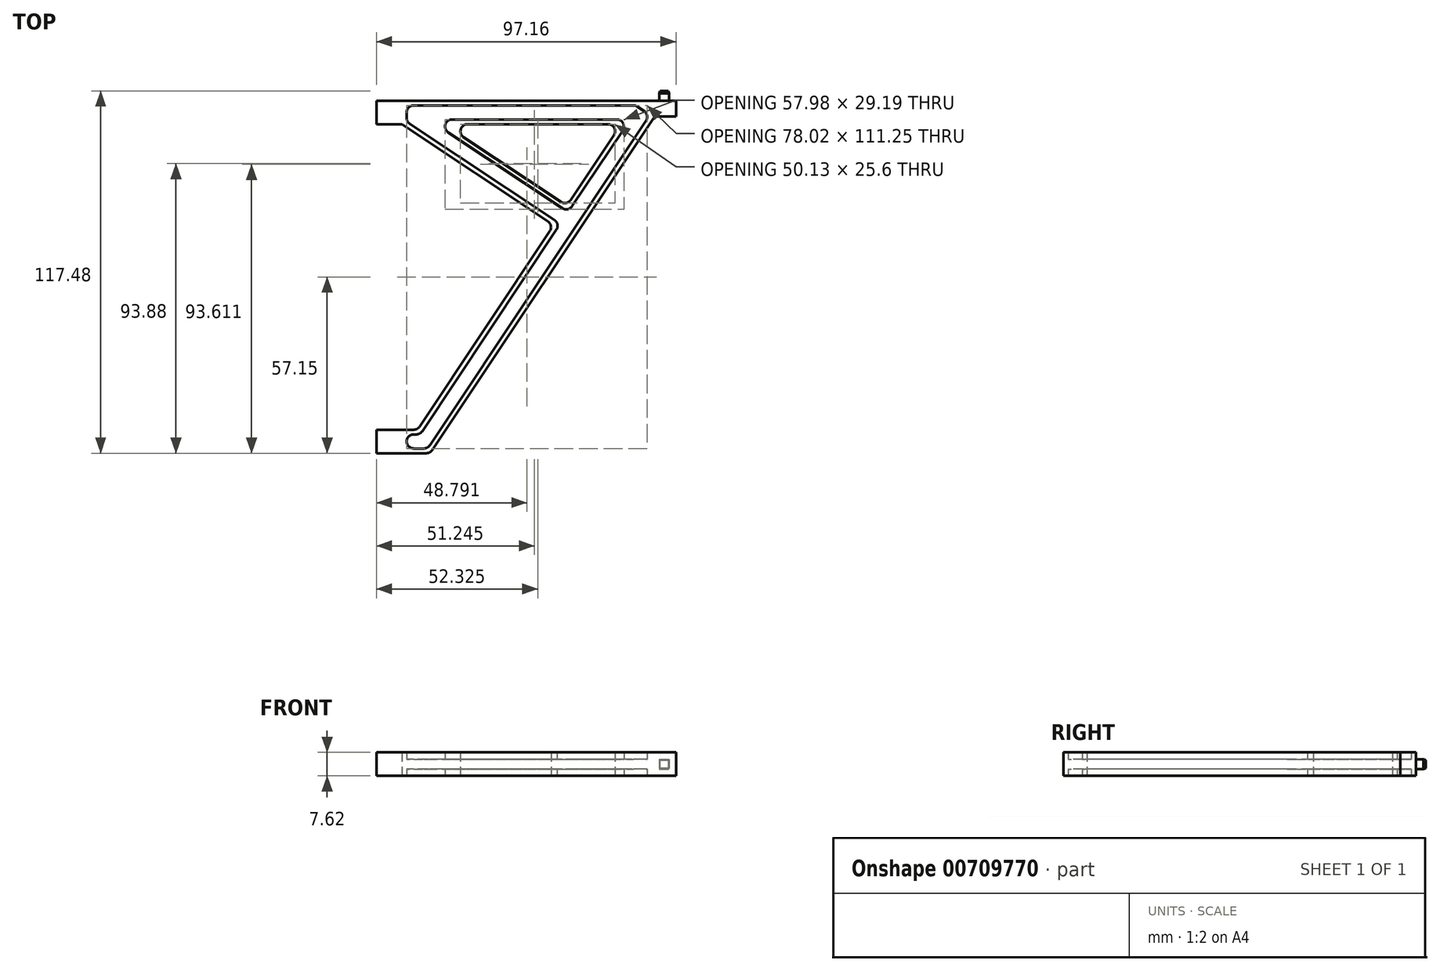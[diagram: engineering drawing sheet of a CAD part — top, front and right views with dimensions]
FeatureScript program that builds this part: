
annotation { "Feature Type Name" : "Feature", "Feature Type Description" : "" }
export const myFeature = defineFeature(function(context is Context, id is Id, definition is map)
    precondition{}
    {
        {
            var Q0;
            Q0=qCreatedBy(makeId("Top.planeOp"),FACE);
            var sketch = newSketch(context, id + "F0", { "sketchPlane" : qUnion([Q0])});
            skLineSegment(sketch, "E0", {"start": v(27.06, 0) * mm, "end": v(27.06, 3.8) * mm});
            skLineSegment(sketch, "E1", {"start": v(32.14, 7.62) * mm, "end": v(76.3, 73.86) * mm});
            skLineSegment(sketch, "E2", {"start": v(103.26, 114.3) * mm, "end": v(27.06, 114.3) * mm});
            skLineSegment(sketch, "E3", {"start": v(103.26, 114.3) * mm, "end": v(109.6, 110.07) * mm});
            skLineSegment(sketch, "E4", {"start": v(109.03, 109.22) * mm, "end": v(36.22, 0) * mm});
            skLineSegment(sketch, "E5", {"start": v(36.22, 0) * mm, "end": v(27.06, 0) * mm});
            skLineSegment(sketch, "E6", {"start": v(40.8, 106.68) * mm, "end": v(98.18, 106.68) * mm});
            skLineSegment(sketch, "E7", {"start": v(27.06, 7.62) * mm, "end": v(32.14, 7.62) * mm});
            skLineSegment(sketch, "E8", {"start": v(40.8, 106.68) * mm, "end": v(80.52, 80.2) * mm});
            skLineSegment(sketch, "E9", {"start": v(27.06, 106.68) * mm, "end": v(76.3, 73.86) * mm});
            skLineSegment(sketch, "E10.trimOffspring", {"start": v(80.52, 80.2) * mm, "end": v(98.18, 106.68) * mm});
            skLineSegment(sketch, "E11", {"start": v(103.26, 114.3) * mm, "end": v(115.96, 114.3) * mm});
            skLineSegment(sketch, "E12", {"start": v(115.96, 114.3) * mm, "end": v(115.96, 109.22) * mm});
            skLineSegment(sketch, "E13", {"start": v(116.43, 109.22) * mm, "end": v(109.03, 109.22) * mm});
            skLineSegment(sketch, "E14", {"start": v(107.48, 109.65) * mm, "end": v(84.79, 75.6) * mm});
            skLineSegment(sketch, "E15", {"start": v(101.03, 108.2) * mm, "end": v(80.98, 78.14) * mm});
            skLineSegment(sketch, "E16.trimOffspring", {"start": v(78.44, 74.33) * mm, "end": v(28.58, 107.5) * mm});
            skLineSegment(sketch, "E17.trimOffspring", {"start": v(80.98, 78.14) * mm, "end": v(35.77, 108.2) * mm});
            skLineSegment(sketch, "E18.trimOffspring", {"start": v(78.44, 74.33) * mm, "end": v(32.95, 6.1) * mm});
            skLineSegment(sketch, "E19.trimOffspring", {"start": v(82.25, 71.8) * mm, "end": v(35.4, 1.52) * mm});
            skLineSegment(sketch, "E20", {"start": v(28.58, 6.1) * mm, "end": v(32.95, 6.1) * mm});
            skLineSegment(sketch, "E21", {"start": v(28.58, 1.52) * mm, "end": v(35.4, 1.52) * mm});
            skLineSegment(sketch, "E22", {"start": v(28.58, 6.1) * mm, "end": v(28.58, 1.52) * mm});
            skLineSegment(sketch, "E23", {"start": v(107.48, 109.65) * mm, "end": v(102.8, 112.78) * mm});
            skLineSegment(sketch, "E24", {"start": v(28.58, 112.78) * mm, "end": v(102.8, 112.78) * mm});
            skLineSegment(sketch, "E25.trimOffspring", {"start": v(35.77, 108.2) * mm, "end": v(101.03, 108.2) * mm});
            skLineSegment(sketch, "E26", {"start": v(28.58, 112.78) * mm, "end": v(28.58, 107.5) * mm});
            skLineSegment(sketch, "E27", {"start": v(82.25, 71.8) * mm, "end": v(84.79, 75.6) * mm});
            skLineSegment(sketch, "E28", {"start": v(27.06, 7.62) * mm, "end": v(18.8, 7.62) * mm});
            skLineSegment(sketch, "E29", {"start": v(18.8, 7.62) * mm, "end": v(18.8, 0) * mm});
            skLineSegment(sketch, "E30", {"start": v(18.8, 0) * mm, "end": v(23.88, 0) * mm});
            skLineSegment(sketch, "E31", {"start": v(23.88, 0) * mm, "end": v(23.88, 3.81) * mm});
            skLineSegment(sketch, "E32", {"start": v(23.88, 3.81) * mm, "end": v(27.06, 3.81) * mm});
            skLineSegment(sketch, "E33.trimOffspring", {"start": v(27.06, 7.62) * mm, "end": v(27.06, 110.49) * mm});
            skLineSegment(sketch, "E34", {"start": v(113.74, 114.3) * mm, "end": v(113.74, 117.48) * mm});
            skLineSegment(sketch, "E35", {"start": v(113.74, 117.48) * mm, "end": v(110.56, 117.48) * mm});
            skLineSegment(sketch, "E36", {"start": v(110.56, 117.48) * mm, "end": v(110.56, 114.3) * mm});
            skLineSegment(sketch, "E37", {"start": v(27.06, 114.3) * mm, "end": v(18.8, 114.3) * mm});
            skLineSegment(sketch, "E38", {"start": v(18.8, 114.3) * mm, "end": v(18.8, 106.68) * mm});
            skLineSegment(sketch, "E39", {"start": v(18.8, 106.68) * mm, "end": v(23.88, 106.68) * mm});
            skLineSegment(sketch, "E40", {"start": v(23.88, 106.68) * mm, "end": v(23.88, 110.49) * mm});
            skLineSegment(sketch, "E41", {"start": v(23.88, 110.49) * mm, "end": v(27.06, 110.49) * mm});
            skLineSegment(sketch, "E42", {"start": v(23.88, 0) * mm, "end": v(27.06, 0) * mm});
            skLineSegment(sketch, "E43", {"start": v(23.88, 106.68) * mm, "end": v(27.06, 106.68) * mm});
            skSolve(sketch);
        }
        {
            var Q0;
            Q0=makeQuery(id+"F0.imprint","IMPRINT",FACE,{"disambiguationData":[TD([[makeQuery(id+"F0.imprint","IMPRINT",EDGE,{"derivedFrom":sQuery(id+"F0.wireOp",EDGE,"E14")}),-1.0]])]});
            extrude(context, id + "F1", {"entities" : qUnion([Q0]), "depth" : 3.17 * mm, "offsetDistance" : 25.4 * mm, "symmetric" : true});
        }
        {
            var Q0;
            Q0=makeQuery(id+"F0.imprint","IMPRINT",FACE,{"disambiguationData":[TD([[makeQuery(id+"F0.imprint","IMPRINT",EDGE,{"derivedFrom":sQuery(id+"F0.wireOp",EDGE,"E0")}),-1.0]])]});
            var Q1;
            Q1=makeQuery(id+"F0.imprint","IMPRINT",FACE,{"disambiguationData":[TD([[makeQuery(id+"F0.imprint","IMPRINT",EDGE,{"derivedFrom":sQuery(id+"F0.wireOp",EDGE,"E6")}),1.0]])]});
            var Q2;
            Q2=makeQuery(id+"F0.imprint","IMPRINT",FACE,{"disambiguationData":[TD([[makeQuery(id+"F0.imprint","IMPRINT",EDGE,{"derivedFrom":sQuery(id+"F0.wireOp",EDGE,"E0")}),1.0]])]});
            var Q3;
            Q3=makeQuery(id+"F0.imprint","IMPRINT",FACE,{"disambiguationData":[TD([[makeQuery(id+"F0.imprint","IMPRINT",EDGE,{"derivedFrom":sQuery(id+"F0.wireOp",EDGE,"E40")}),-1.0]])]});
            extrude(context, id + "F2", {"entities" : qUnion([Q0, Q1, Q2, Q3]), "operationType" : NewBodyOperationType.ADD, "depth" : 7.62 * mm, "offsetDistance" : 25.4 * mm, "symmetric" : true});
        }
        {
            var Q0;
            {var subQ0=sQuery(id+"F0.wireOp",EDGE,"E34");Q0=makeQuery(id+"F0.imprint","IMPRINT",FACE,{"disambiguationData":[TD([[makeQuery(id+"F0.imprint","IMPRINT",EDGE,{"derivedFrom":subQ0}),1.0]])]});}
            extrude(context, id + "F3", {"entities" : qUnion([Q0]), "operationType" : NewBodyOperationType.ADD, "depth" : 3.17 * mm, "offsetDistance" : 25.4 * mm, "symmetric" : true});
        }
        {
            var Q0;
            Q0=makeQuery(id+"F1.opExtrude","SWEPT_BODY",BODY,{"disambiguationData":[OSD([sQuery(id+"F0.wireOp",EDGE,"E14"),sQuery(id+"F0.wireOp",EDGE,"E15"),sQuery(id+"F0.wireOp",EDGE,"E16.trimOffspring"),sQuery(id+"F0.wireOp",EDGE,"E17.trimOffspring"),sQuery(id+"F0.wireOp",EDGE,"E18.trimOffspring"),sQuery(id+"F0.wireOp",EDGE,"E19.trimOffspring"),sQuery(id+"F0.wireOp",EDGE,"E20"),sQuery(id+"F0.wireOp",EDGE,"E21"),sQuery(id+"F0.wireOp",EDGE,"E22"),sQuery(id+"F0.wireOp",EDGE,"E23"),sQuery(id+"F0.wireOp",EDGE,"E24"),sQuery(id+"F0.wireOp",EDGE,"E25.trimOffspring"),sQuery(id+"F0.wireOp",EDGE,"E26"),sQuery(id+"F0.wireOp",EDGE,"E27")])]});
            transform(context, id + "F4", {"entities" : qUnion([Q0]), "transformType" : TransformType.TRANSLATION_3D, "dx" : 0 * mm, "dy" : 0 * mm, "dz" : 3.8 * mm, "makeCopy" : false});
        }
        {
            var Q0;
            Q0=makeQuery(id+"F2.opExtrude","SWEPT_EDGE",EDGE,{"disambiguationData":[OSD([sQuery(id+"F0.wireOp",EDGE,"E1"),sQuery(id+"F0.wireOp",EDGE,"E9")])]});
            var Q1;
            Q1=makeQuery(id+"F2.opExtrude","SWEPT_EDGE",EDGE,{"disambiguationData":[OSD([sQuery(id+"F0.wireOp",EDGE,"E8"),sQuery(id+"F0.wireOp",EDGE,"E10.trimOffspring")])]});
            var Q2;
            Q2=makeQuery(id+"F2.opExtrude","SWEPT_EDGE",EDGE,{"disambiguationData":[OSD([sQuery(id+"F0.wireOp",EDGE,"E6"),sQuery(id+"F0.wireOp",EDGE,"E10.trimOffspring")])]});
            var Q3;
            Q3=makeQuery(id+"F2.opExtrude","SWEPT_EDGE",EDGE,{"disambiguationData":[OSD([sQuery(id+"F0.wireOp",EDGE,"E6"),sQuery(id+"F0.wireOp",EDGE,"E8")])]});
            var Q4;
            {var subQ0=sQuery(id+"F0.wireOp",EDGE,"E25.trimOffspring");var subQ1=sQuery(id+"F0.wireOp",EDGE,"E17.trimOffspring");var subQ2=sQuery(id+"F0.wireOp",EDGE,"E15");Q4=makeQuery(id+"F2.boolean.opBoolean","SPLIT",EDGE,{"disambiguationData":[TD([makeQuery(id+"F2.opExtrude","CAP_FACE",FACE,{"disambiguationData":[OSD([sQuery(id+"F0.wireOp",EDGE,"E6"),sQuery(id+"F0.wireOp",EDGE,"E8"),sQuery(id+"F0.wireOp",EDGE,"E10.trimOffspring"),subQ2,subQ1,subQ0])],"isStart":false})])],"derivedFrom":makeQuery(id+"F2.opExtrude","SWEPT_EDGE",EDGE,{"disambiguationData":[OSD([subQ1,subQ0])]})});}
            var Q5;
            {var subQ0=sQuery(id+"F0.wireOp",EDGE,"E25.trimOffspring");var subQ1=sQuery(id+"F0.wireOp",EDGE,"E17.trimOffspring");var subQ2=sQuery(id+"F0.wireOp",EDGE,"E15");Q5=makeQuery(id+"F2.boolean.opBoolean","SPLIT",EDGE,{"disambiguationData":[TD([makeQuery(id+"F2.opExtrude","CAP_FACE",FACE,{"disambiguationData":[OSD([sQuery(id+"F0.wireOp",EDGE,"E6"),sQuery(id+"F0.wireOp",EDGE,"E8"),sQuery(id+"F0.wireOp",EDGE,"E10.trimOffspring"),subQ2,subQ1,subQ0])],"isStart":true})])],"derivedFrom":makeQuery(id+"F2.opExtrude","SWEPT_EDGE",EDGE,{"disambiguationData":[OSD([subQ1,subQ0])]})});}
            var Q6;
            {var subQ0=sQuery(id+"F0.wireOp",EDGE,"E25.trimOffspring");var subQ1=sQuery(id+"F0.wireOp",EDGE,"E17.trimOffspring");var subQ2=sQuery(id+"F0.wireOp",EDGE,"E15");Q6=makeQuery(id+"F2.boolean.opBoolean","SPLIT",EDGE,{"disambiguationData":[TD([makeQuery(id+"F2.opExtrude","CAP_FACE",FACE,{"disambiguationData":[OSD([sQuery(id+"F0.wireOp",EDGE,"E6"),sQuery(id+"F0.wireOp",EDGE,"E8"),sQuery(id+"F0.wireOp",EDGE,"E10.trimOffspring"),subQ2,subQ1,subQ0])],"isStart":false})])],"derivedFrom":makeQuery(id+"F2.opExtrude","SWEPT_EDGE",EDGE,{"disambiguationData":[OSD([subQ2,subQ0])]})});}
            var Q7;
            {var subQ0=sQuery(id+"F0.wireOp",EDGE,"E25.trimOffspring");var subQ1=sQuery(id+"F0.wireOp",EDGE,"E17.trimOffspring");var subQ2=sQuery(id+"F0.wireOp",EDGE,"E15");Q7=makeQuery(id+"F2.boolean.opBoolean","SPLIT",EDGE,{"disambiguationData":[TD([makeQuery(id+"F2.opExtrude","CAP_FACE",FACE,{"disambiguationData":[OSD([sQuery(id+"F0.wireOp",EDGE,"E6"),sQuery(id+"F0.wireOp",EDGE,"E8"),sQuery(id+"F0.wireOp",EDGE,"E10.trimOffspring"),subQ2,subQ1,subQ0])],"isStart":true})])],"derivedFrom":makeQuery(id+"F2.opExtrude","SWEPT_EDGE",EDGE,{"disambiguationData":[OSD([subQ2,subQ0])]})});}
            var Q8;
            {var subQ0=sQuery(id+"F0.wireOp",EDGE,"E25.trimOffspring");var subQ1=sQuery(id+"F0.wireOp",EDGE,"E17.trimOffspring");var subQ2=sQuery(id+"F0.wireOp",EDGE,"E15");Q8=makeQuery(id+"F2.boolean.opBoolean","SPLIT",EDGE,{"disambiguationData":[TD([makeQuery(id+"F2.opExtrude","CAP_FACE",FACE,{"disambiguationData":[OSD([sQuery(id+"F0.wireOp",EDGE,"E6"),sQuery(id+"F0.wireOp",EDGE,"E8"),sQuery(id+"F0.wireOp",EDGE,"E10.trimOffspring"),subQ2,subQ1,subQ0])],"isStart":true})])],"derivedFrom":makeQuery(id+"F2.opExtrude","SWEPT_EDGE",EDGE,{"disambiguationData":[OSD([subQ2,subQ1])]})});}
            var Q9;
            {var subQ0=sQuery(id+"F0.wireOp",EDGE,"E25.trimOffspring");var subQ1=sQuery(id+"F0.wireOp",EDGE,"E17.trimOffspring");var subQ2=sQuery(id+"F0.wireOp",EDGE,"E15");Q9=makeQuery(id+"F2.boolean.opBoolean","SPLIT",EDGE,{"disambiguationData":[TD([makeQuery(id+"F2.opExtrude","CAP_FACE",FACE,{"disambiguationData":[OSD([sQuery(id+"F0.wireOp",EDGE,"E6"),sQuery(id+"F0.wireOp",EDGE,"E8"),sQuery(id+"F0.wireOp",EDGE,"E10.trimOffspring"),subQ2,subQ1,subQ0])],"isStart":false})])],"derivedFrom":makeQuery(id+"F2.opExtrude","SWEPT_EDGE",EDGE,{"disambiguationData":[OSD([subQ2,subQ1])]})});}
            var Q10;
            {var subQ0=sQuery(id+"F0.wireOp",EDGE,"E27");var subQ1=sQuery(id+"F0.wireOp",EDGE,"E26");var subQ2=sQuery(id+"F0.wireOp",EDGE,"E24");var subQ3=sQuery(id+"F0.wireOp",EDGE,"E23");var subQ4=sQuery(id+"F0.wireOp",EDGE,"E22");var subQ5=sQuery(id+"F0.wireOp",EDGE,"E21");var subQ6=sQuery(id+"F0.wireOp",EDGE,"E20");var subQ7=sQuery(id+"F0.wireOp",EDGE,"E19.trimOffspring");var subQ8=sQuery(id+"F0.wireOp",EDGE,"E18.trimOffspring");var subQ9=sQuery(id+"F0.wireOp",EDGE,"E16.trimOffspring");var subQ10=sQuery(id+"F0.wireOp",EDGE,"E14");Q10=makeQuery(id+"F2.boolean.opBoolean","SPLIT",EDGE,{"disambiguationData":[TD([makeQuery(id+"F1.opExtrude","CAP_FACE",FACE,{"disambiguationData":[OSD([subQ10,sQuery(id+"F0.wireOp",EDGE,"E15"),subQ9,sQuery(id+"F0.wireOp",EDGE,"E17.trimOffspring"),subQ8,subQ7,subQ6,subQ5,subQ4,subQ3,subQ2,sQuery(id+"F0.wireOp",EDGE,"E25.trimOffspring"),subQ1,subQ0])],"isStart":false})])],"derivedFrom":makeQuery(id+"F2.opExtrude","SWEPT_EDGE",EDGE,{"disambiguationData":[OSD([subQ9,subQ8])]})});}
            var Q11;
            {var subQ0=sQuery(id+"F0.wireOp",EDGE,"E27");var subQ1=sQuery(id+"F0.wireOp",EDGE,"E26");var subQ2=sQuery(id+"F0.wireOp",EDGE,"E24");var subQ3=sQuery(id+"F0.wireOp",EDGE,"E23");var subQ4=sQuery(id+"F0.wireOp",EDGE,"E22");var subQ5=sQuery(id+"F0.wireOp",EDGE,"E21");var subQ6=sQuery(id+"F0.wireOp",EDGE,"E20");var subQ7=sQuery(id+"F0.wireOp",EDGE,"E19.trimOffspring");var subQ8=sQuery(id+"F0.wireOp",EDGE,"E18.trimOffspring");var subQ9=sQuery(id+"F0.wireOp",EDGE,"E16.trimOffspring");var subQ10=sQuery(id+"F0.wireOp",EDGE,"E14");Q11=makeQuery(id+"F2.boolean.opBoolean","SPLIT",EDGE,{"disambiguationData":[TD([makeQuery(id+"F1.opExtrude","CAP_FACE",FACE,{"disambiguationData":[OSD([subQ10,sQuery(id+"F0.wireOp",EDGE,"E15"),subQ9,sQuery(id+"F0.wireOp",EDGE,"E17.trimOffspring"),subQ8,subQ7,subQ6,subQ5,subQ4,subQ3,subQ2,sQuery(id+"F0.wireOp",EDGE,"E25.trimOffspring"),subQ1,subQ0])],"isStart":true})])],"derivedFrom":makeQuery(id+"F2.opExtrude","SWEPT_EDGE",EDGE,{"disambiguationData":[OSD([subQ9,subQ8])]})});}
            var Q12;
            {var subQ0=sQuery(id+"F0.wireOp",EDGE,"E27");var subQ1=sQuery(id+"F0.wireOp",EDGE,"E26");var subQ2=sQuery(id+"F0.wireOp",EDGE,"E24");var subQ3=sQuery(id+"F0.wireOp",EDGE,"E23");var subQ4=sQuery(id+"F0.wireOp",EDGE,"E22");var subQ5=sQuery(id+"F0.wireOp",EDGE,"E21");var subQ6=sQuery(id+"F0.wireOp",EDGE,"E20");var subQ7=sQuery(id+"F0.wireOp",EDGE,"E19.trimOffspring");var subQ8=sQuery(id+"F0.wireOp",EDGE,"E18.trimOffspring");var subQ9=sQuery(id+"F0.wireOp",EDGE,"E16.trimOffspring");var subQ10=sQuery(id+"F0.wireOp",EDGE,"E14");Q12=makeQuery(id+"F2.boolean.opBoolean","SPLIT",EDGE,{"disambiguationData":[TD([makeQuery(id+"F1.opExtrude","CAP_FACE",FACE,{"disambiguationData":[OSD([subQ10,sQuery(id+"F0.wireOp",EDGE,"E15"),subQ9,sQuery(id+"F0.wireOp",EDGE,"E17.trimOffspring"),subQ8,subQ7,subQ6,subQ5,subQ4,subQ3,subQ2,sQuery(id+"F0.wireOp",EDGE,"E25.trimOffspring"),subQ1,subQ0])],"isStart":false})])],"derivedFrom":makeQuery(id+"F2.opExtrude","SWEPT_EDGE",EDGE,{"disambiguationData":[OSD([subQ3,subQ2])]})});}
            var Q13;
            {var subQ0=sQuery(id+"F0.wireOp",EDGE,"E27");var subQ1=sQuery(id+"F0.wireOp",EDGE,"E26");var subQ2=sQuery(id+"F0.wireOp",EDGE,"E24");var subQ3=sQuery(id+"F0.wireOp",EDGE,"E23");var subQ4=sQuery(id+"F0.wireOp",EDGE,"E22");var subQ5=sQuery(id+"F0.wireOp",EDGE,"E21");var subQ6=sQuery(id+"F0.wireOp",EDGE,"E20");var subQ7=sQuery(id+"F0.wireOp",EDGE,"E19.trimOffspring");var subQ8=sQuery(id+"F0.wireOp",EDGE,"E18.trimOffspring");var subQ9=sQuery(id+"F0.wireOp",EDGE,"E16.trimOffspring");var subQ10=sQuery(id+"F0.wireOp",EDGE,"E14");Q13=makeQuery(id+"F2.boolean.opBoolean","SPLIT",EDGE,{"disambiguationData":[TD([makeQuery(id+"F1.opExtrude","CAP_FACE",FACE,{"disambiguationData":[OSD([subQ10,sQuery(id+"F0.wireOp",EDGE,"E15"),subQ9,sQuery(id+"F0.wireOp",EDGE,"E17.trimOffspring"),subQ8,subQ7,subQ6,subQ5,subQ4,subQ3,subQ2,sQuery(id+"F0.wireOp",EDGE,"E25.trimOffspring"),subQ1,subQ0])],"isStart":true})])],"derivedFrom":makeQuery(id+"F2.opExtrude","SWEPT_EDGE",EDGE,{"disambiguationData":[OSD([subQ3,subQ2])]})});}
            var Q14;
            {var subQ0=sQuery(id+"F0.wireOp",EDGE,"E27");var subQ1=sQuery(id+"F0.wireOp",EDGE,"E26");var subQ2=sQuery(id+"F0.wireOp",EDGE,"E24");var subQ3=sQuery(id+"F0.wireOp",EDGE,"E23");var subQ4=sQuery(id+"F0.wireOp",EDGE,"E22");var subQ5=sQuery(id+"F0.wireOp",EDGE,"E21");var subQ6=sQuery(id+"F0.wireOp",EDGE,"E20");var subQ7=sQuery(id+"F0.wireOp",EDGE,"E19.trimOffspring");var subQ8=sQuery(id+"F0.wireOp",EDGE,"E18.trimOffspring");var subQ9=sQuery(id+"F0.wireOp",EDGE,"E16.trimOffspring");var subQ10=sQuery(id+"F0.wireOp",EDGE,"E14");Q14=makeQuery(id+"F2.boolean.opBoolean","SPLIT",EDGE,{"disambiguationData":[TD([makeQuery(id+"F1.opExtrude","CAP_FACE",FACE,{"disambiguationData":[OSD([subQ10,sQuery(id+"F0.wireOp",EDGE,"E15"),subQ9,sQuery(id+"F0.wireOp",EDGE,"E17.trimOffspring"),subQ8,subQ7,subQ6,subQ5,subQ4,subQ3,subQ2,sQuery(id+"F0.wireOp",EDGE,"E25.trimOffspring"),subQ1,subQ0])],"isStart":false})])],"derivedFrom":makeQuery(id+"F2.opExtrude","SWEPT_EDGE",EDGE,{"disambiguationData":[OSD([subQ2,subQ1])]})});}
            var Q15;
            {var subQ0=sQuery(id+"F0.wireOp",EDGE,"E27");var subQ1=sQuery(id+"F0.wireOp",EDGE,"E26");var subQ2=sQuery(id+"F0.wireOp",EDGE,"E24");var subQ3=sQuery(id+"F0.wireOp",EDGE,"E23");var subQ4=sQuery(id+"F0.wireOp",EDGE,"E22");var subQ5=sQuery(id+"F0.wireOp",EDGE,"E21");var subQ6=sQuery(id+"F0.wireOp",EDGE,"E20");var subQ7=sQuery(id+"F0.wireOp",EDGE,"E19.trimOffspring");var subQ8=sQuery(id+"F0.wireOp",EDGE,"E18.trimOffspring");var subQ9=sQuery(id+"F0.wireOp",EDGE,"E16.trimOffspring");var subQ10=sQuery(id+"F0.wireOp",EDGE,"E14");Q15=makeQuery(id+"F2.boolean.opBoolean","SPLIT",EDGE,{"disambiguationData":[TD([makeQuery(id+"F1.opExtrude","CAP_FACE",FACE,{"disambiguationData":[OSD([subQ10,sQuery(id+"F0.wireOp",EDGE,"E15"),subQ9,sQuery(id+"F0.wireOp",EDGE,"E17.trimOffspring"),subQ8,subQ7,subQ6,subQ5,subQ4,subQ3,subQ2,sQuery(id+"F0.wireOp",EDGE,"E25.trimOffspring"),subQ1,subQ0])],"isStart":false})])],"derivedFrom":makeQuery(id+"F2.opExtrude","SWEPT_EDGE",EDGE,{"disambiguationData":[OSD([subQ9,subQ1])]})});}
            var Q16;
            {var subQ0=sQuery(id+"F0.wireOp",EDGE,"E27");var subQ1=sQuery(id+"F0.wireOp",EDGE,"E26");var subQ2=sQuery(id+"F0.wireOp",EDGE,"E24");var subQ3=sQuery(id+"F0.wireOp",EDGE,"E23");var subQ4=sQuery(id+"F0.wireOp",EDGE,"E22");var subQ5=sQuery(id+"F0.wireOp",EDGE,"E21");var subQ6=sQuery(id+"F0.wireOp",EDGE,"E20");var subQ7=sQuery(id+"F0.wireOp",EDGE,"E19.trimOffspring");var subQ8=sQuery(id+"F0.wireOp",EDGE,"E18.trimOffspring");var subQ9=sQuery(id+"F0.wireOp",EDGE,"E16.trimOffspring");var subQ10=sQuery(id+"F0.wireOp",EDGE,"E14");Q16=makeQuery(id+"F2.boolean.opBoolean","SPLIT",EDGE,{"disambiguationData":[TD([makeQuery(id+"F1.opExtrude","CAP_FACE",FACE,{"disambiguationData":[OSD([subQ10,sQuery(id+"F0.wireOp",EDGE,"E15"),subQ9,sQuery(id+"F0.wireOp",EDGE,"E17.trimOffspring"),subQ8,subQ7,subQ6,subQ5,subQ4,subQ3,subQ2,sQuery(id+"F0.wireOp",EDGE,"E25.trimOffspring"),subQ1,subQ0])],"isStart":true})])],"derivedFrom":makeQuery(id+"F2.opExtrude","SWEPT_EDGE",EDGE,{"disambiguationData":[OSD([subQ9,subQ1])]})});}
            var Q17;
            {var subQ0=sQuery(id+"F0.wireOp",EDGE,"E27");var subQ1=sQuery(id+"F0.wireOp",EDGE,"E26");var subQ2=sQuery(id+"F0.wireOp",EDGE,"E24");var subQ3=sQuery(id+"F0.wireOp",EDGE,"E23");var subQ4=sQuery(id+"F0.wireOp",EDGE,"E22");var subQ5=sQuery(id+"F0.wireOp",EDGE,"E21");var subQ6=sQuery(id+"F0.wireOp",EDGE,"E20");var subQ7=sQuery(id+"F0.wireOp",EDGE,"E19.trimOffspring");var subQ8=sQuery(id+"F0.wireOp",EDGE,"E18.trimOffspring");var subQ9=sQuery(id+"F0.wireOp",EDGE,"E16.trimOffspring");var subQ10=sQuery(id+"F0.wireOp",EDGE,"E14");Q17=makeQuery(id+"F2.boolean.opBoolean","SPLIT",EDGE,{"disambiguationData":[TD([makeQuery(id+"F1.opExtrude","CAP_FACE",FACE,{"disambiguationData":[OSD([subQ10,sQuery(id+"F0.wireOp",EDGE,"E15"),subQ9,sQuery(id+"F0.wireOp",EDGE,"E17.trimOffspring"),subQ8,subQ7,subQ6,subQ5,subQ4,subQ3,subQ2,sQuery(id+"F0.wireOp",EDGE,"E25.trimOffspring"),subQ1,subQ0])],"isStart":true})])],"derivedFrom":makeQuery(id+"F2.opExtrude","SWEPT_EDGE",EDGE,{"disambiguationData":[OSD([subQ2,subQ1])]})});}
            var Q18;
            Q18=makeQuery(id+"F2.opExtrude","SWEPT_EDGE",EDGE,{"disambiguationData":[OSD([sQuery(id+"F0.wireOp",EDGE,"E4"),sQuery(id+"F0.wireOp",EDGE,"E13")])]});
            var Q19;
            Q19=makeQuery(id+"F2.opExtrude","SWEPT_EDGE",EDGE,{"disambiguationData":[OSD([sQuery(id+"F0.wireOp",EDGE,"E1"),sQuery(id+"F0.wireOp",EDGE,"E7")])]});
            var Q20;
            Q20=makeQuery(id+"F2.opExtrude","SWEPT_EDGE",EDGE,{"disambiguationData":[OSD([sQuery(id+"F0.wireOp",EDGE,"E4"),sQuery(id+"F0.wireOp",EDGE,"E5")])]});
            var Q21;
            {var subQ0=sQuery(id+"F0.wireOp",EDGE,"E27");var subQ1=sQuery(id+"F0.wireOp",EDGE,"E26");var subQ2=sQuery(id+"F0.wireOp",EDGE,"E24");var subQ3=sQuery(id+"F0.wireOp",EDGE,"E23");var subQ4=sQuery(id+"F0.wireOp",EDGE,"E22");var subQ5=sQuery(id+"F0.wireOp",EDGE,"E21");var subQ6=sQuery(id+"F0.wireOp",EDGE,"E20");var subQ7=sQuery(id+"F0.wireOp",EDGE,"E19.trimOffspring");var subQ8=sQuery(id+"F0.wireOp",EDGE,"E18.trimOffspring");var subQ9=sQuery(id+"F0.wireOp",EDGE,"E16.trimOffspring");var subQ10=sQuery(id+"F0.wireOp",EDGE,"E14");Q21=makeQuery(id+"F2.boolean.opBoolean","SPLIT",EDGE,{"disambiguationData":[TD([makeQuery(id+"F1.opExtrude","CAP_FACE",FACE,{"disambiguationData":[OSD([subQ10,sQuery(id+"F0.wireOp",EDGE,"E15"),subQ9,sQuery(id+"F0.wireOp",EDGE,"E17.trimOffspring"),subQ8,subQ7,subQ6,subQ5,subQ4,subQ3,subQ2,sQuery(id+"F0.wireOp",EDGE,"E25.trimOffspring"),subQ1,subQ0])],"isStart":false})])],"derivedFrom":makeQuery(id+"F2.opExtrude","SWEPT_EDGE",EDGE,{"disambiguationData":[OSD([subQ8,subQ6])]})});}
            var Q22;
            {var subQ0=sQuery(id+"F0.wireOp",EDGE,"E27");var subQ1=sQuery(id+"F0.wireOp",EDGE,"E26");var subQ2=sQuery(id+"F0.wireOp",EDGE,"E24");var subQ3=sQuery(id+"F0.wireOp",EDGE,"E23");var subQ4=sQuery(id+"F0.wireOp",EDGE,"E22");var subQ5=sQuery(id+"F0.wireOp",EDGE,"E21");var subQ6=sQuery(id+"F0.wireOp",EDGE,"E20");var subQ7=sQuery(id+"F0.wireOp",EDGE,"E19.trimOffspring");var subQ8=sQuery(id+"F0.wireOp",EDGE,"E18.trimOffspring");var subQ9=sQuery(id+"F0.wireOp",EDGE,"E16.trimOffspring");var subQ10=sQuery(id+"F0.wireOp",EDGE,"E14");Q22=makeQuery(id+"F2.boolean.opBoolean","SPLIT",EDGE,{"disambiguationData":[TD([makeQuery(id+"F1.opExtrude","CAP_FACE",FACE,{"disambiguationData":[OSD([subQ10,sQuery(id+"F0.wireOp",EDGE,"E15"),subQ9,sQuery(id+"F0.wireOp",EDGE,"E17.trimOffspring"),subQ8,subQ7,subQ6,subQ5,subQ4,subQ3,subQ2,sQuery(id+"F0.wireOp",EDGE,"E25.trimOffspring"),subQ1,subQ0])],"isStart":true})])],"derivedFrom":makeQuery(id+"F2.opExtrude","SWEPT_EDGE",EDGE,{"disambiguationData":[OSD([subQ8,subQ6])]})});}
            var Q23;
            {var subQ0=sQuery(id+"F0.wireOp",EDGE,"E27");var subQ1=sQuery(id+"F0.wireOp",EDGE,"E26");var subQ2=sQuery(id+"F0.wireOp",EDGE,"E24");var subQ3=sQuery(id+"F0.wireOp",EDGE,"E23");var subQ4=sQuery(id+"F0.wireOp",EDGE,"E22");var subQ5=sQuery(id+"F0.wireOp",EDGE,"E21");var subQ6=sQuery(id+"F0.wireOp",EDGE,"E20");var subQ7=sQuery(id+"F0.wireOp",EDGE,"E19.trimOffspring");var subQ8=sQuery(id+"F0.wireOp",EDGE,"E18.trimOffspring");var subQ9=sQuery(id+"F0.wireOp",EDGE,"E16.trimOffspring");var subQ10=sQuery(id+"F0.wireOp",EDGE,"E14");Q23=makeQuery(id+"F2.boolean.opBoolean","SPLIT",EDGE,{"disambiguationData":[TD([makeQuery(id+"F1.opExtrude","CAP_FACE",FACE,{"disambiguationData":[OSD([subQ10,sQuery(id+"F0.wireOp",EDGE,"E15"),subQ9,sQuery(id+"F0.wireOp",EDGE,"E17.trimOffspring"),subQ8,subQ7,subQ6,subQ5,subQ4,subQ3,subQ2,sQuery(id+"F0.wireOp",EDGE,"E25.trimOffspring"),subQ1,subQ0])],"isStart":true})])],"derivedFrom":makeQuery(id+"F2.opExtrude","SWEPT_EDGE",EDGE,{"disambiguationData":[OSD([subQ7,subQ5])]})});}
            var Q24;
            {var subQ0=sQuery(id+"F0.wireOp",EDGE,"E27");var subQ1=sQuery(id+"F0.wireOp",EDGE,"E26");var subQ2=sQuery(id+"F0.wireOp",EDGE,"E24");var subQ3=sQuery(id+"F0.wireOp",EDGE,"E23");var subQ4=sQuery(id+"F0.wireOp",EDGE,"E22");var subQ5=sQuery(id+"F0.wireOp",EDGE,"E21");var subQ6=sQuery(id+"F0.wireOp",EDGE,"E20");var subQ7=sQuery(id+"F0.wireOp",EDGE,"E19.trimOffspring");var subQ8=sQuery(id+"F0.wireOp",EDGE,"E18.trimOffspring");var subQ9=sQuery(id+"F0.wireOp",EDGE,"E16.trimOffspring");var subQ10=sQuery(id+"F0.wireOp",EDGE,"E14");Q24=makeQuery(id+"F2.boolean.opBoolean","SPLIT",EDGE,{"disambiguationData":[TD([makeQuery(id+"F1.opExtrude","CAP_FACE",FACE,{"disambiguationData":[OSD([subQ10,sQuery(id+"F0.wireOp",EDGE,"E15"),subQ9,sQuery(id+"F0.wireOp",EDGE,"E17.trimOffspring"),subQ8,subQ7,subQ6,subQ5,subQ4,subQ3,subQ2,sQuery(id+"F0.wireOp",EDGE,"E25.trimOffspring"),subQ1,subQ0])],"isStart":false})])],"derivedFrom":makeQuery(id+"F2.opExtrude","SWEPT_EDGE",EDGE,{"disambiguationData":[OSD([subQ7,subQ5])]})});}
            var Q25;
            {var subQ0=sQuery(id+"F0.wireOp",EDGE,"E27");var subQ1=sQuery(id+"F0.wireOp",EDGE,"E26");var subQ2=sQuery(id+"F0.wireOp",EDGE,"E24");var subQ3=sQuery(id+"F0.wireOp",EDGE,"E23");var subQ4=sQuery(id+"F0.wireOp",EDGE,"E22");var subQ5=sQuery(id+"F0.wireOp",EDGE,"E21");var subQ6=sQuery(id+"F0.wireOp",EDGE,"E20");var subQ7=sQuery(id+"F0.wireOp",EDGE,"E19.trimOffspring");var subQ8=sQuery(id+"F0.wireOp",EDGE,"E18.trimOffspring");var subQ9=sQuery(id+"F0.wireOp",EDGE,"E16.trimOffspring");var subQ10=sQuery(id+"F0.wireOp",EDGE,"E14");Q25=makeQuery(id+"F2.boolean.opBoolean","SPLIT",EDGE,{"disambiguationData":[TD([makeQuery(id+"F1.opExtrude","CAP_FACE",FACE,{"disambiguationData":[OSD([subQ10,sQuery(id+"F0.wireOp",EDGE,"E15"),subQ9,sQuery(id+"F0.wireOp",EDGE,"E17.trimOffspring"),subQ8,subQ7,subQ6,subQ5,subQ4,subQ3,subQ2,sQuery(id+"F0.wireOp",EDGE,"E25.trimOffspring"),subQ1,subQ0])],"isStart":false})])],"derivedFrom":makeQuery(id+"F2.opExtrude","SWEPT_EDGE",EDGE,{"disambiguationData":[OSD([subQ6,subQ4])]})});}
            var Q26;
            {var subQ0=sQuery(id+"F0.wireOp",EDGE,"E27");var subQ1=sQuery(id+"F0.wireOp",EDGE,"E26");var subQ2=sQuery(id+"F0.wireOp",EDGE,"E24");var subQ3=sQuery(id+"F0.wireOp",EDGE,"E23");var subQ4=sQuery(id+"F0.wireOp",EDGE,"E22");var subQ5=sQuery(id+"F0.wireOp",EDGE,"E21");var subQ6=sQuery(id+"F0.wireOp",EDGE,"E20");var subQ7=sQuery(id+"F0.wireOp",EDGE,"E19.trimOffspring");var subQ8=sQuery(id+"F0.wireOp",EDGE,"E18.trimOffspring");var subQ9=sQuery(id+"F0.wireOp",EDGE,"E16.trimOffspring");var subQ10=sQuery(id+"F0.wireOp",EDGE,"E14");Q26=makeQuery(id+"F2.boolean.opBoolean","SPLIT",EDGE,{"disambiguationData":[TD([makeQuery(id+"F1.opExtrude","CAP_FACE",FACE,{"disambiguationData":[OSD([subQ10,sQuery(id+"F0.wireOp",EDGE,"E15"),subQ9,sQuery(id+"F0.wireOp",EDGE,"E17.trimOffspring"),subQ8,subQ7,subQ6,subQ5,subQ4,subQ3,subQ2,sQuery(id+"F0.wireOp",EDGE,"E25.trimOffspring"),subQ1,subQ0])],"isStart":false})])],"derivedFrom":makeQuery(id+"F2.opExtrude","SWEPT_EDGE",EDGE,{"disambiguationData":[OSD([subQ5,subQ4])]})});}
            var Q27;
            {var subQ0=sQuery(id+"F0.wireOp",EDGE,"E27");var subQ1=sQuery(id+"F0.wireOp",EDGE,"E26");var subQ2=sQuery(id+"F0.wireOp",EDGE,"E24");var subQ3=sQuery(id+"F0.wireOp",EDGE,"E23");var subQ4=sQuery(id+"F0.wireOp",EDGE,"E22");var subQ5=sQuery(id+"F0.wireOp",EDGE,"E21");var subQ6=sQuery(id+"F0.wireOp",EDGE,"E20");var subQ7=sQuery(id+"F0.wireOp",EDGE,"E19.trimOffspring");var subQ8=sQuery(id+"F0.wireOp",EDGE,"E18.trimOffspring");var subQ9=sQuery(id+"F0.wireOp",EDGE,"E16.trimOffspring");var subQ10=sQuery(id+"F0.wireOp",EDGE,"E14");Q27=makeQuery(id+"F2.boolean.opBoolean","SPLIT",EDGE,{"disambiguationData":[TD([makeQuery(id+"F1.opExtrude","CAP_FACE",FACE,{"disambiguationData":[OSD([subQ10,sQuery(id+"F0.wireOp",EDGE,"E15"),subQ9,sQuery(id+"F0.wireOp",EDGE,"E17.trimOffspring"),subQ8,subQ7,subQ6,subQ5,subQ4,subQ3,subQ2,sQuery(id+"F0.wireOp",EDGE,"E25.trimOffspring"),subQ1,subQ0])],"isStart":true})])],"derivedFrom":makeQuery(id+"F2.opExtrude","SWEPT_EDGE",EDGE,{"disambiguationData":[OSD([subQ5,subQ4])]})});}
            var Q28;
            {var subQ0=sQuery(id+"F0.wireOp",EDGE,"E27");var subQ1=sQuery(id+"F0.wireOp",EDGE,"E26");var subQ2=sQuery(id+"F0.wireOp",EDGE,"E24");var subQ3=sQuery(id+"F0.wireOp",EDGE,"E23");var subQ4=sQuery(id+"F0.wireOp",EDGE,"E22");var subQ5=sQuery(id+"F0.wireOp",EDGE,"E21");var subQ6=sQuery(id+"F0.wireOp",EDGE,"E20");var subQ7=sQuery(id+"F0.wireOp",EDGE,"E19.trimOffspring");var subQ8=sQuery(id+"F0.wireOp",EDGE,"E18.trimOffspring");var subQ9=sQuery(id+"F0.wireOp",EDGE,"E16.trimOffspring");var subQ10=sQuery(id+"F0.wireOp",EDGE,"E14");Q28=makeQuery(id+"F2.boolean.opBoolean","SPLIT",EDGE,{"disambiguationData":[TD([makeQuery(id+"F1.opExtrude","CAP_FACE",FACE,{"disambiguationData":[OSD([subQ10,sQuery(id+"F0.wireOp",EDGE,"E15"),subQ9,sQuery(id+"F0.wireOp",EDGE,"E17.trimOffspring"),subQ8,subQ7,subQ6,subQ5,subQ4,subQ3,subQ2,sQuery(id+"F0.wireOp",EDGE,"E25.trimOffspring"),subQ1,subQ0])],"isStart":true})])],"derivedFrom":makeQuery(id+"F2.opExtrude","SWEPT_EDGE",EDGE,{"disambiguationData":[OSD([subQ6,subQ4])]})});}
            var Q29;
            {var subQ0=sQuery(id+"F0.wireOp",EDGE,"E27");var subQ1=sQuery(id+"F0.wireOp",EDGE,"E26");var subQ2=sQuery(id+"F0.wireOp",EDGE,"E24");var subQ3=sQuery(id+"F0.wireOp",EDGE,"E23");var subQ4=sQuery(id+"F0.wireOp",EDGE,"E22");var subQ5=sQuery(id+"F0.wireOp",EDGE,"E21");var subQ6=sQuery(id+"F0.wireOp",EDGE,"E20");var subQ7=sQuery(id+"F0.wireOp",EDGE,"E19.trimOffspring");var subQ8=sQuery(id+"F0.wireOp",EDGE,"E18.trimOffspring");var subQ9=sQuery(id+"F0.wireOp",EDGE,"E16.trimOffspring");var subQ10=sQuery(id+"F0.wireOp",EDGE,"E14");Q29=makeQuery(id+"F2.boolean.opBoolean","SPLIT",EDGE,{"disambiguationData":[TD([makeQuery(id+"F1.opExtrude","CAP_FACE",FACE,{"disambiguationData":[OSD([subQ10,sQuery(id+"F0.wireOp",EDGE,"E15"),subQ9,sQuery(id+"F0.wireOp",EDGE,"E17.trimOffspring"),subQ8,subQ7,subQ6,subQ5,subQ4,subQ3,subQ2,sQuery(id+"F0.wireOp",EDGE,"E25.trimOffspring"),subQ1,subQ0])],"isStart":false})])],"derivedFrom":makeQuery(id+"F2.opExtrude","SWEPT_EDGE",EDGE,{"disambiguationData":[OSD([subQ10,subQ3])]})});}
            var Q30;
            {var subQ0=sQuery(id+"F0.wireOp",EDGE,"E27");var subQ1=sQuery(id+"F0.wireOp",EDGE,"E26");var subQ2=sQuery(id+"F0.wireOp",EDGE,"E24");var subQ3=sQuery(id+"F0.wireOp",EDGE,"E23");var subQ4=sQuery(id+"F0.wireOp",EDGE,"E22");var subQ5=sQuery(id+"F0.wireOp",EDGE,"E21");var subQ6=sQuery(id+"F0.wireOp",EDGE,"E20");var subQ7=sQuery(id+"F0.wireOp",EDGE,"E19.trimOffspring");var subQ8=sQuery(id+"F0.wireOp",EDGE,"E18.trimOffspring");var subQ9=sQuery(id+"F0.wireOp",EDGE,"E16.trimOffspring");var subQ10=sQuery(id+"F0.wireOp",EDGE,"E14");Q30=makeQuery(id+"F2.boolean.opBoolean","SPLIT",EDGE,{"disambiguationData":[TD([makeQuery(id+"F1.opExtrude","CAP_FACE",FACE,{"disambiguationData":[OSD([subQ10,sQuery(id+"F0.wireOp",EDGE,"E15"),subQ9,sQuery(id+"F0.wireOp",EDGE,"E17.trimOffspring"),subQ8,subQ7,subQ6,subQ5,subQ4,subQ3,subQ2,sQuery(id+"F0.wireOp",EDGE,"E25.trimOffspring"),subQ1,subQ0])],"isStart":true})])],"derivedFrom":makeQuery(id+"F2.opExtrude","SWEPT_EDGE",EDGE,{"disambiguationData":[OSD([subQ10,subQ3])]})});}
            fillet(context, id + "F5", {"entities" : qUnion([Q0, Q1, Q2, Q3, Q4, Q5, Q6, Q7, Q8, Q9, Q10, Q11, Q12, Q13, Q14, Q15, Q16, Q17, Q18, Q19, Q20, Q21, Q22, Q23, Q24, Q25, Q26, Q27, Q28, Q29, Q30]), "radius" : 2.3 * mm, "tangentPropagation" : true, "allowEdgeOverflow" : false});
        }
        {
            var Q0;
            Q0=makeQuery(id+"F3.opExtrude","SWEPT_FACE",FACE,{"disambiguationData":[OSD([sQuery(id+"F0.wireOp",EDGE,"E35")])]});
            chamfer(context, id + "F6", {"entities" : qUnion([Q0]), "chamferType" : ChamferType.TWO_OFFSETS, "width1" : 0.25 * mm, "oppositeDirection" : false, "width2" : 0.76 * mm, "tangentPropagation" : true});
        }
    });
